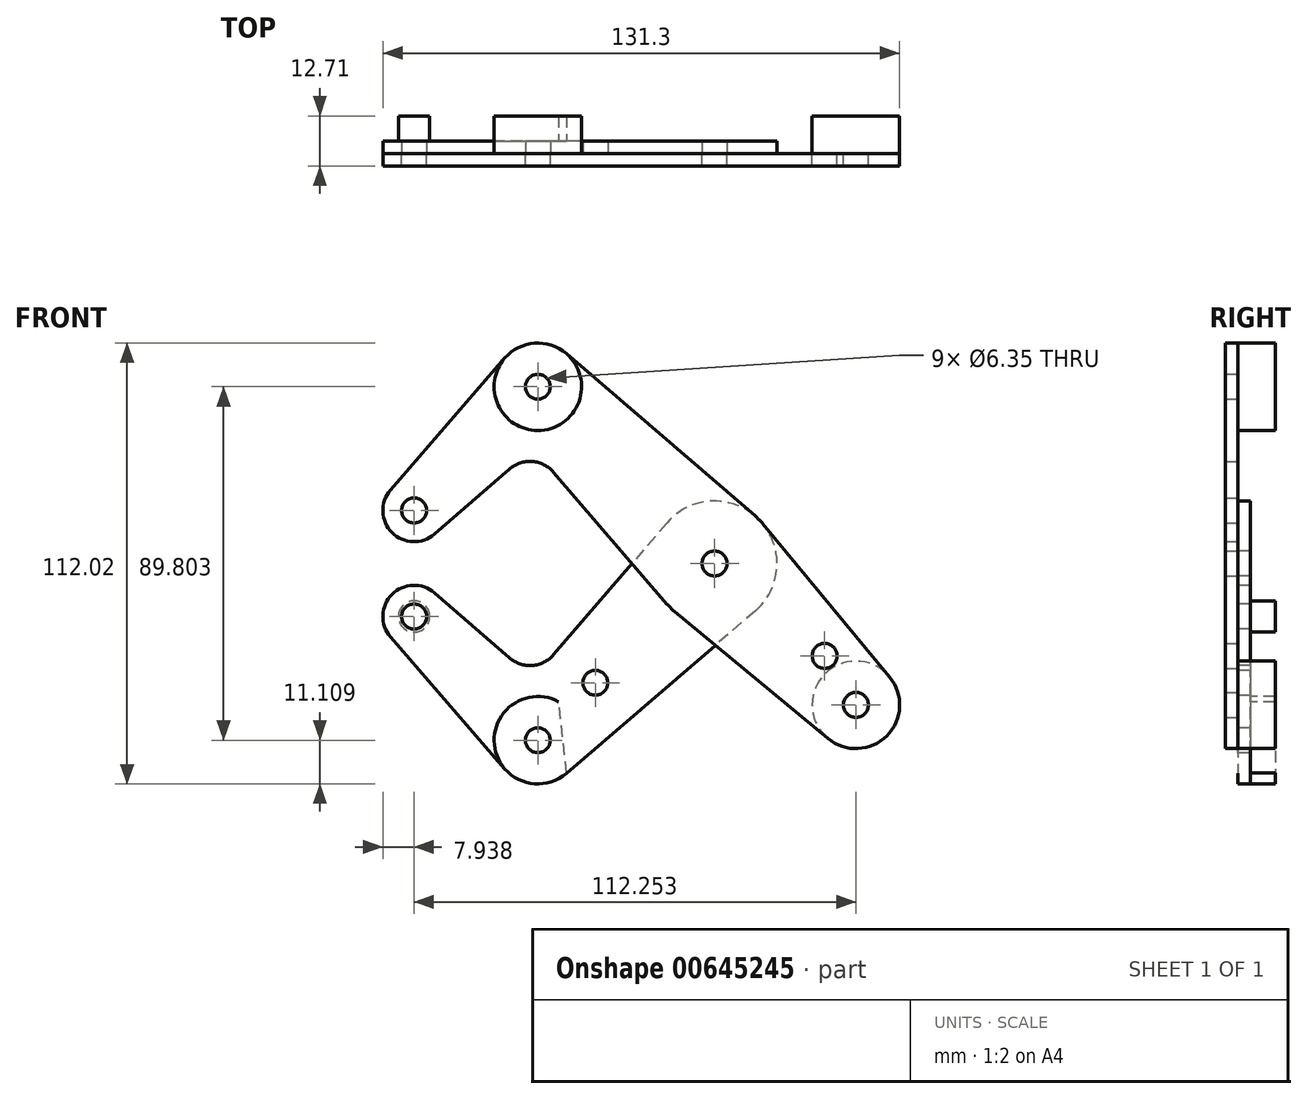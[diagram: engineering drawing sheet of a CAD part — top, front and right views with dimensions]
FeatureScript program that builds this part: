
annotation { "Feature Type Name" : "Feature", "Feature Type Description" : "" }
export const myFeature = defineFeature(function(context is Context, id is Id, definition is map)
    precondition{}
    {
        {
            var Q0;
            Q0=qCreatedBy(makeId("Front.planeOp"),FACE);
            var sketch = newSketch(context, id + "F0", { "sketchPlane" : qUnion([Q0])});
            skLineSegment(sketch, "E0", {"start": v(-76.33, 13.47) * mm, "end": v(-44.9, 44.9) * mm, "construction": true});
            skLineSegment(sketch, "E1", {"start": v(-44.9, 44.9) * mm, "end": v(35.92, -35.92) * mm, "construction": true});
            skCircle(sketch, "E2", {"center": v(-76.33, 13.47) * mm, "radius": 3.18 * mm});
            skCircle(sketch, "E3", {"center": v(-76.33, 13.47) * mm, "radius": 7.94 * mm});
            skCircle(sketch, "E4", {"center": v(-44.9, 44.9) * mm, "radius": 11.11 * mm});
            skCircle(sketch, "E5", {"center": v(-44.9, 44.9) * mm, "radius": 3.18 * mm});
            skCircle(sketch, "E6", {"center": v(0, 0) * mm, "radius": 15.88 * mm});
            skCircle(sketch, "E7", {"center": v(0, 0) * mm, "radius": 3.98 * mm});
            skCircle(sketch, "E8", {"center": v(0, 0) * mm, "radius": 3.18 * mm});
            skCircle(sketch, "E9", {"center": v(35.92, -35.92) * mm, "radius": 11.11 * mm});
            skCircle(sketch, "E10", {"center": v(35.92, -35.92) * mm, "radius": 3.18 * mm});
            skCircle(sketch, "E11", {"center": v(27.97, -23.48) * mm, "radius": 3.18 * mm});
            skLineSegment(sketch, "E12", {"start": v(-10.12, -12.23) * mm, "end": v(28.83, -44.48) * mm});
            skLineSegment(sketch, "E13", {"start": v(12.23, 10.12) * mm, "end": v(44.48, -28.83) * mm});
            skLineSegment(sketch, "E14", {"start": v(-71.13, 7.47) * mm, "end": v(-52.08, 23.98) * mm});
            skLineSegment(sketch, "E15", {"start": v(-12.04, -10.35) * mm, "end": v(-40.85, 23.15) * mm});
            skLineSegment(sketch, "E16", {"start": v(-37.66, 53.33) * mm, "end": v(10.35, 12.04) * mm});
            skLineSegment(sketch, "E17", {"start": v(-53.3, 52.18) * mm, "end": v(-82.33, 18.67) * mm});
            skArc(sketch, "E18.filletArc", {"start": v(-40.85, 23.15) * mm, "mid": v(-46.3, 25.9) * mm, "end": v(-52.08, 23.98) * mm});
            skLineSegment(sketch, "E19", {"start": v(0, 0) * mm, "end": v(-44.9, -44.9) * mm, "construction": true});
            skLineSegment(sketch, "E20", {"start": v(-44.9, -44.9) * mm, "end": v(-76.33, -13.47) * mm, "construction": true});
            skCircle(sketch, "E21", {"center": v(-44.9, -44.9) * mm, "radius": 3.18 * mm});
            skCircle(sketch, "E22", {"center": v(-44.9, -44.9) * mm, "radius": 11.11 * mm});
            skCircle(sketch, "E23", {"center": v(-76.33, -13.47) * mm, "radius": 3.18 * mm});
            skCircle(sketch, "E24", {"center": v(-76.33, -13.47) * mm, "radius": 7.94 * mm});
            skCircle(sketch, "E25", {"center": v(-30.3, -30.3) * mm, "radius": 3.18 * mm});
            skLineSegment(sketch, "E26", {"start": v(-82.33, -18.67) * mm, "end": v(-53.3, -52.18) * mm});
            skLineSegment(sketch, "E27", {"start": v(-71.13, -7.47) * mm, "end": v(-52.08, -23.98) * mm});
            skLineSegment(sketch, "E28", {"start": v(-12.04, 10.35) * mm, "end": v(-40.85, -23.15) * mm});
            skLineSegment(sketch, "E29", {"start": v(10.35, -12.04) * mm, "end": v(-37.66, -53.33) * mm});
            skArc(sketch, "E30.filletArc", {"start": v(-52.08, -23.98) * mm, "mid": v(-46.3, -25.9) * mm, "end": v(-40.85, -23.15) * mm});
            skSolve(sketch);
        }
        {
            var Q0;
            {var subQ0=sQuery(id+"F0.wireOp",EDGE,"E14");Q0=makeQuery(id+"F0.imprint","IMPRINT",FACE,{"disambiguationData":[TD([[makeQuery(id+"F0.imprint","IMPRINT",EDGE,{"derivedFrom":subQ0}),1.0]])]});}
            var Q1;
            Q1=makeQuery(id+"F0.imprint","IMPRINT",FACE,{"disambiguationData":[TD([[makeQuery(id+"F0.imprint","IMPRINT",EDGE,{"derivedFrom":sQuery(id+"F0.wireOp",EDGE,"E5")}),-1.0]])]});
            var Q2;
            Q2=makeQuery(id+"F0.imprint","IMPRINT",FACE,{"disambiguationData":[TD([[makeQuery(id+"F0.imprint","IMPRINT",EDGE,{"derivedFrom":sQuery(id+"F0.wireOp",EDGE,"E2")}),-1.0]])]});
            var Q3;
            Q3=makeQuery(id+"F0.imprint","IMPRINT",FACE,{"disambiguationData":[TD([[makeQuery(id+"F0.imprint","IMPRINT",EDGE,{"derivedFrom":sQuery(id+"F0.wireOp",EDGE,"E7")}),-1.0]])]});
            var Q4;
            Q4=makeQuery(id+"F0.imprint","IMPRINT",FACE,{"disambiguationData":[TD([[makeQuery(id+"F0.imprint","IMPRINT",EDGE,{"derivedFrom":sQuery(id+"F0.wireOp",EDGE,"E11")}),-1.0]])]});
            var Q5;
            Q5=makeQuery(id+"F0.imprint","IMPRINT",FACE,{"disambiguationData":[TD([[makeQuery(id+"F0.imprint","IMPRINT",EDGE,{"derivedFrom":sQuery(id+"F0.wireOp",EDGE,"E10")}),-1.0]])]});
            var Q6;
            {var subQ0=sQuery(id+"F0.wireOp",EDGE,"E12");var subQ1=sQuery(id+"F0.wireOp",EDGE,"E6");var subQ2=makeQuery(id+"F0.imprint","INTERSECT",VERTEX,{"derivedFrom":[subQ1,subQ0]});Q6=makeQuery(id+"F0.imprint","IMPRINT",FACE,{"disambiguationData":[TD([[makeQuery(id+"F0.imprint","IMPRINT",EDGE,{"disambiguationData":[TD([[subQ2,-1.0]])],"derivedFrom":subQ1}),-1.0]])]});}
            var Q7;
            {var subQ0=sQuery(id+"F0.wireOp",EDGE,"E15");var subQ1=sQuery(id+"F0.wireOp",EDGE,"E6");var subQ2=makeQuery(id+"F0.imprint","INTERSECT",VERTEX,{"derivedFrom":[subQ1,subQ0]});Q7=makeQuery(id+"F0.imprint","IMPRINT",FACE,{"disambiguationData":[TD([[makeQuery(id+"F0.imprint","IMPRINT",EDGE,{"disambiguationData":[TD([[subQ2,1.0]])],"derivedFrom":subQ1}),-1.0]])]});}
            var Q8;
            Q8=makeQuery(id+"F0.imprint","IMPRINT",FACE,{"disambiguationData":[TD([[makeQuery(id+"F0.imprint","IMPRINT",EDGE,{"derivedFrom":sQuery(id+"F0.wireOp",EDGE,"E7")}),1.0]])]});
            extrude(context, id + "F1", {"entities" : qUnion([Q0, Q1, Q2, Q3, Q4, Q5, Q6, Q7, Q8]), "depth" : 3.17 * mm, "offsetDistance" : 25.4 * mm});
        }
        {
            var Q0;
            Q0=makeQuery(id+"F0.imprint","IMPRINT",FACE,{"disambiguationData":[TD([[makeQuery(id+"F0.imprint","IMPRINT",EDGE,{"derivedFrom":sQuery(id+"F0.wireOp",EDGE,"E25")}),-1.0]])]});
            var Q1;
            Q1=makeQuery(id+"F0.imprint","IMPRINT",FACE,{"disambiguationData":[TD([[makeQuery(id+"F0.imprint","IMPRINT",EDGE,{"derivedFrom":sQuery(id+"F0.wireOp",EDGE,"E21")}),-1.0]])]});
            var Q2;
            Q2=makeQuery(id+"F0.imprint","IMPRINT",FACE,{"disambiguationData":[TD([[makeQuery(id+"F0.imprint","IMPRINT",EDGE,{"derivedFrom":sQuery(id+"F0.wireOp",EDGE,"E23")}),-1.0]])]});
            var Q3;
            Q3=makeQuery(id+"F0.imprint","IMPRINT",FACE,{"disambiguationData":[TD([[makeQuery(id+"F0.imprint","IMPRINT",EDGE,{"derivedFrom":sQuery(id+"F0.wireOp",EDGE,"E7")}),-1.0]])]});
            var Q4;
            {var subQ0=sQuery(id+"F0.wireOp",EDGE,"E15");var subQ1=sQuery(id+"F0.wireOp",EDGE,"E6");var subQ2=makeQuery(id+"F0.imprint","INTERSECT",VERTEX,{"derivedFrom":[subQ1,subQ0]});Q4=makeQuery(id+"F0.imprint","IMPRINT",FACE,{"disambiguationData":[TD([[makeQuery(id+"F0.imprint","IMPRINT",EDGE,{"disambiguationData":[TD([[subQ2,1.0]])],"derivedFrom":subQ1}),-1.0]])]});}
            var Q5;
            {var subQ0=sQuery(id+"F0.wireOp",EDGE,"E12");var subQ1=sQuery(id+"F0.wireOp",EDGE,"E6");var subQ2=makeQuery(id+"F0.imprint","INTERSECT",VERTEX,{"derivedFrom":[subQ1,subQ0]});Q5=makeQuery(id+"F0.imprint","IMPRINT",FACE,{"disambiguationData":[TD([[makeQuery(id+"F0.imprint","IMPRINT",EDGE,{"disambiguationData":[TD([[subQ2,-1.0]])],"derivedFrom":subQ1}),-1.0]])]});}
            var Q6;
            Q6=makeQuery(id+"F0.imprint","IMPRINT",FACE,{"disambiguationData":[TD([[makeQuery(id+"F0.imprint","IMPRINT",EDGE,{"derivedFrom":sQuery(id+"F0.wireOp",EDGE,"E7")}),1.0]])]});
            extrude(context, id + "F2", {"entities" : qUnion([Q0, Q1, Q2, Q3, Q4, Q5, Q6]), "oppositeDirection" : true, "depth" : 3.17 * mm, "offsetDistance" : 25.4 * mm});
        }
        {
            var Q0;
            Q0=qCreatedBy(makeId("Front.planeOp"),FACE);
            var sketch = newSketch(context, id + "F3", { "sketchPlane" : qUnion([Q0])});
            skArc(sketch, "E31.0", {"start": v(-39.6, -35.14) * mm, "mid": v(-55.95, -46.13) * mm, "end": v(-37.58, -53.26) * mm});
            skPoint(sketch, "E32.0", {"position": v(35.92, -35.92) * mm});
            skLineSegment(sketch, "E33", {"start": v(35.92, -35.92) * mm, "end": v(-44.9, -44.9) * mm, "construction": true});
            skCircle(sketch, "E34.0", {"center": v(35.92, -35.92) * mm, "radius": 11.11 * mm});
            skPoint(sketch, "E35.0", {"position": v(-76.33, -13.47) * mm});
            skPoint(sketch, "E36.0", {"position": v(-44.9, 44.9) * mm});
            skCircle(sketch, "E37", {"center": v(-44.9, 44.9) * mm, "radius": 3.98 * mm});
            skCircle(sketch, "E38", {"center": v(-76.33, -13.47) * mm, "radius": 3.98 * mm});
            skLineSegment(sketch, "E39", {"start": v(-39.6, -35.14) * mm, "end": v(-37.58, -53.26) * mm});
            skPoint(sketch, "E40", {"position": v(-38.6, -44.2) * mm});
            skSolve(sketch);
        }
        {
            var Q0;
            Q0=qCreatedBy(makeId("Front.planeOp"),FACE);
            cPlane(context, id + "F4", {"entities" : qUnion([Q0]), "cplaneType" : CPlaneType.OFFSET, "offset" : 9.52 * mm, "oppositeDirection" : true, "width" : 152.4 * mm, "height" : 152.4 * mm});
        }
        {
            var Q0;
            Q0=makeQuery(id+"F3.imprint","IMPRINT",FACE,{"disambiguationData":[TD([[makeQuery(id+"F3.imprint","IMPRINT",EDGE,{"derivedFrom":sQuery(id+"F3.wireOp",EDGE,"E31.0")}),1.0]])]});
            var Q1;
            Q1=makeQuery(id+"F3.imprint","IMPRINT",FACE,{"disambiguationData":[TD([[makeQuery(id+"F3.imprint","IMPRINT",EDGE,{"derivedFrom":sQuery(id+"F3.wireOp",EDGE,"E38")}),1.0]])]});
            var Q2;
            Q2=qCreatedBy(id+"F4.planeOp",FACE);
            extrude(context, id + "F5", {"entities" : qUnion([Q0, Q1]), "endBound" : BoundingType.UP_TO_SURFACE, "oppositeDirection" : true, "depth" : 25.4 * mm, "endBoundEntityFace" : qUnion([Q2]), "offsetDistance" : 25.4 * mm});
        }
        {
            var Q0;
            Q0=makeQuery(id+"F1.opExtrude","CAP_FACE",FACE,{"disambiguationData":[OSD([sQuery(id+"F0.wireOp",EDGE,"E2"),sQuery(id+"F0.wireOp",EDGE,"E3"),sQuery(id+"F0.wireOp",EDGE,"E4"),sQuery(id+"F0.wireOp",EDGE,"E5"),sQuery(id+"F0.wireOp",EDGE,"E6"),sQuery(id+"F0.wireOp",EDGE,"E8"),sQuery(id+"F0.wireOp",EDGE,"E9"),sQuery(id+"F0.wireOp",EDGE,"E10"),sQuery(id+"F0.wireOp",EDGE,"E11"),sQuery(id+"F0.wireOp",EDGE,"E12"),sQuery(id+"F0.wireOp",EDGE,"E13"),sQuery(id+"F0.wireOp",EDGE,"E14"),sQuery(id+"F0.wireOp",EDGE,"E15"),sQuery(id+"F0.wireOp",EDGE,"E16"),sQuery(id+"F0.wireOp",EDGE,"E17"),sQuery(id+"F0.wireOp",EDGE,"E18.filletArc")])],"isStart":false});
            var sketch = newSketch(context, id + "F6", { "sketchPlane" : qUnion([Q0])});
            skCircle(sketch, "E41.0", {"center": v(35.92, -35.92) * mm, "radius": 11.11 * mm});
            skCircle(sketch, "E42.0", {"center": v(-44.9, 44.9) * mm, "radius": 11.11 * mm});
            skSolve(sketch);
        }
        {
            var Q0;
            Q0 = qSketchRegion(id + "F6", true);
            var Q1;
            Q1=qCreatedBy(id+"F4.planeOp",FACE);
            extrude(context, id + "F7", {"entities" : qUnion([Q0]), "endBound" : BoundingType.UP_TO_SURFACE, "oppositeDirection" : true, "depth" : 25.4 * mm, "endBoundEntityFace" : qUnion([Q1]), "offsetDistance" : 25.4 * mm});
        }
        {
            var Q0;
            Q0=makeQuery(id+"F1.opExtrude","SWEPT_BODY",BODY,{"disambiguationData":[OSD([sQuery(id+"F0.wireOp",EDGE,"E2"),sQuery(id+"F0.wireOp",EDGE,"E3"),sQuery(id+"F0.wireOp",EDGE,"E4"),sQuery(id+"F0.wireOp",EDGE,"E5"),sQuery(id+"F0.wireOp",EDGE,"E6"),sQuery(id+"F0.wireOp",EDGE,"E8"),sQuery(id+"F0.wireOp",EDGE,"E9"),sQuery(id+"F0.wireOp",EDGE,"E10"),sQuery(id+"F0.wireOp",EDGE,"E11"),sQuery(id+"F0.wireOp",EDGE,"E12"),sQuery(id+"F0.wireOp",EDGE,"E13"),sQuery(id+"F0.wireOp",EDGE,"E14"),sQuery(id+"F0.wireOp",EDGE,"E15"),sQuery(id+"F0.wireOp",EDGE,"E16"),sQuery(id+"F0.wireOp",EDGE,"E17"),sQuery(id+"F0.wireOp",EDGE,"E18.filletArc")])]});
            var Q1;
            Q1=makeQuery(id+"F7.opExtrude","SWEPT_BODY",BODY,{"disambiguationData":[OSD([sQuery(id+"F6.wireOp",EDGE,"E41.0")])]});
            booleanBodies(context, id + "F8", {"operationType" : BooleanOperationType.SUBTRACTION, "tools" : qUnion([Q0]), "targets" : qUnion([Q1]), "keepTools" : true});
        }
        {
            var Q0;
            Q0=makeQuery(id+"F1.opExtrude","SWEPT_BODY",BODY,{"disambiguationData":[OSD([sQuery(id+"F0.wireOp",EDGE,"E2"),sQuery(id+"F0.wireOp",EDGE,"E3"),sQuery(id+"F0.wireOp",EDGE,"E4"),sQuery(id+"F0.wireOp",EDGE,"E5"),sQuery(id+"F0.wireOp",EDGE,"E6"),sQuery(id+"F0.wireOp",EDGE,"E8"),sQuery(id+"F0.wireOp",EDGE,"E9"),sQuery(id+"F0.wireOp",EDGE,"E10"),sQuery(id+"F0.wireOp",EDGE,"E11"),sQuery(id+"F0.wireOp",EDGE,"E12"),sQuery(id+"F0.wireOp",EDGE,"E13"),sQuery(id+"F0.wireOp",EDGE,"E14"),sQuery(id+"F0.wireOp",EDGE,"E15"),sQuery(id+"F0.wireOp",EDGE,"E16"),sQuery(id+"F0.wireOp",EDGE,"E17"),sQuery(id+"F0.wireOp",EDGE,"E18.filletArc")])]});
            var Q1;
            Q1=makeQuery(id+"F7.opExtrude","SWEPT_BODY",BODY,{"disambiguationData":[OSD([sQuery(id+"F6.wireOp",EDGE,"E42.0")])]});
            booleanBodies(context, id + "F9", {"operationType" : BooleanOperationType.SUBTRACTION, "tools" : qUnion([Q0]), "targets" : qUnion([Q1]), "keepTools" : true});
        }
        {
            var Q0;
            Q0=makeQuery(id+"F2.opExtrude","SWEPT_BODY",BODY,{"disambiguationData":[OSD([sQuery(id+"F0.wireOp",EDGE,"E6"),sQuery(id+"F0.wireOp",EDGE,"E8"),sQuery(id+"F0.wireOp",EDGE,"E21"),sQuery(id+"F0.wireOp",EDGE,"E22"),sQuery(id+"F0.wireOp",EDGE,"E23"),sQuery(id+"F0.wireOp",EDGE,"E24"),sQuery(id+"F0.wireOp",EDGE,"E25"),sQuery(id+"F0.wireOp",EDGE,"E26"),sQuery(id+"F0.wireOp",EDGE,"E27"),sQuery(id+"F0.wireOp",EDGE,"E28"),sQuery(id+"F0.wireOp",EDGE,"E29"),sQuery(id+"F0.wireOp",EDGE,"E30.filletArc")])]});
            var Q1;
            Q1=makeQuery(id+"F5.opExtrude","SWEPT_BODY",BODY,{"disambiguationData":[OSD([sQuery(id+"F3.wireOp",EDGE,"E31.0"),sQuery(id+"F3.wireOp",EDGE,"E39")])]});
            booleanBodies(context, id + "F10", {"operationType" : BooleanOperationType.SUBTRACTION, "tools" : qUnion([Q0]), "targets" : qUnion([Q1]), "keepTools" : true});
        }
        {
            var Q0;
            Q0=makeQuery(id+"F2.opExtrude","SWEPT_BODY",BODY,{"disambiguationData":[OSD([sQuery(id+"F0.wireOp",EDGE,"E6"),sQuery(id+"F0.wireOp",EDGE,"E8"),sQuery(id+"F0.wireOp",EDGE,"E21"),sQuery(id+"F0.wireOp",EDGE,"E22"),sQuery(id+"F0.wireOp",EDGE,"E23"),sQuery(id+"F0.wireOp",EDGE,"E24"),sQuery(id+"F0.wireOp",EDGE,"E25"),sQuery(id+"F0.wireOp",EDGE,"E26"),sQuery(id+"F0.wireOp",EDGE,"E27"),sQuery(id+"F0.wireOp",EDGE,"E28"),sQuery(id+"F0.wireOp",EDGE,"E29"),sQuery(id+"F0.wireOp",EDGE,"E30.filletArc")])]});
            var Q1;
            Q1=makeQuery(id+"F5.opExtrude","SWEPT_BODY",BODY,{"disambiguationData":[OSD([sQuery(id+"F3.wireOp",EDGE,"E38")])]});
            booleanBodies(context, id + "F11", {"operationType" : BooleanOperationType.SUBTRACTION, "tools" : qUnion([Q0]), "targets" : qUnion([Q1]), "keepTools" : true});
        }
    });
